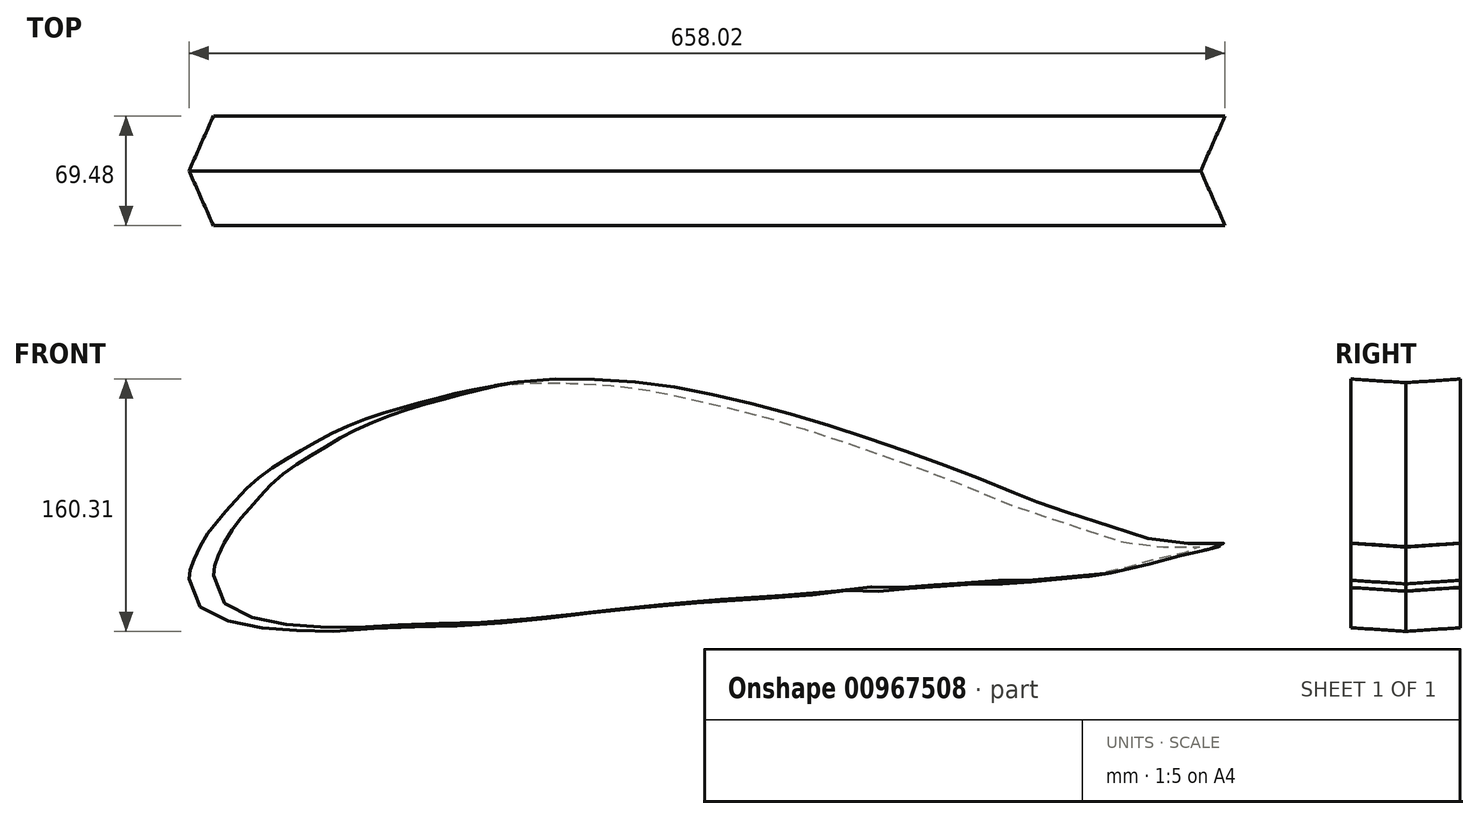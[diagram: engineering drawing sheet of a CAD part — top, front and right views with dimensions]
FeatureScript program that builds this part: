
annotation { "Feature Type Name" : "Feature", "Feature Type Description" : "" }
export const myFeature = defineFeature(function(context is Context, id is Id, definition is map)
    precondition{}
    {
        {
            var Q0;
            Q0=qCreatedBy(makeId("Front.planeOp"),FACE);
            var sketch = newSketch(context, id + "F0", { "sketchPlane" : qUnion([Q0])});
            skFitSpline(sketch, "E0", {"points": [v(4.05, 45.31) * mm, v(5.78, 54.54) * mm, v(15, 73) * mm, v(28.27, 89.14) * mm, v(45.57, 107.6) * mm, v(69.8, 123.74) * mm, v(96.32, 138.73) * mm, v(129.76, 151.42) * mm, v(163.21, 160.64) * mm, v(201.85, 168.72) * mm, v(240.48, 169.87) * mm, v(284.3, 166.99) * mm, v(323.52, 159.5) * mm, v(366.2, 149.11) * mm, v(407.72, 136.42) * mm, v(448.08, 122.58) * mm, v(486.14, 108.75) * mm, v(519.67, 94.87) * mm, v(531.8, 90.25) * mm, v(577.47, 75.22) * mm, v(615.05, 65.97) * mm, v(646.55, 65.4) * mm, v(633.55, 61.34) * mm, v(611, 56.14) * mm, v(577.47, 47.47) * mm, v(527.76, 42.85) * mm, v(519.67, 42.27) * mm, v(503.48, 42.27) * mm, v(481.52, 40.54) * mm, v(463.02, 39.38) * mm, v(444.52, 37.64) * mm, v(424.87, 38.22) * mm, v(404.64, 35.91) * mm, v(343.94, 31.29) * mm, v(280.36, 26.08) * mm, v(239.9, 21.46) * mm, v(201.16, 17.41) * mm, v(162.43, 15.1) * mm, v(130.06, 14.52) * mm, v(97.7, 12.21) * mm, v(71.08, 12.8) * mm, v(48.06, 14.52) * mm, v(25.62, 19.7) * mm, v(10.08, 28.9) * mm, v(4.05, 45.31) * mm]});
            skSolve(sketch);
        }
        {
            var Q0;
            Q0=qCreatedBy(makeId("Top.planeOp"),FACE);
            var sketch = newSketch(context, id + "F1", { "sketchPlane" : qUnion([Q0])});
            skLineSegment(sketch, "E1", {"start": v(4.05, -110.52) * mm, "end": v(4.05, 165.75) * mm, "construction": true});
            skPoint(sketch, "E2", {"position": v(4.05, 0) * mm});
            skLineSegment(sketch, "E3", {"start": v(4.05, 0) * mm, "end": v(18.19, 31.75) * mm});
            skLineSegment(sketch, "E4", {"start": v(4.05, 0) * mm, "end": v(134.8, 0) * mm, "construction": true});
            skLineSegment(sketch, "E5", {"start": v(18.19, 0) * mm, "end": v(18.19, 31.75) * mm, "construction": true});
            skSolve(sketch);
        }
        {
            var Q0;
            Q0=sQuery(id+"F1.wireOp",EDGE,"E3");
            var Q1;
            Q1=sQuery(id+"F1.wireOp",EDGE,"E1");
            cPlane(context, id + "F2", {"entities" : qUnion([Q0, Q1]), "cplaneType" : CPlaneType.LINE_ANGLE, "offset" : 25.4 * mm, "angle" : 90 * degree, "width" : 152.4 * mm, "height" : 152.4 * mm});
        }
        {
            var Q0;
            Q0=qCreatedBy(id+"F2.planeOp",FACE);
            var sketch = newSketch(context, id + "F3", { "sketchPlane" : qUnion([Q0])});
            skLineSegment(sketch, "E6.0", {"start": v(1.65, 0) * mm, "end": v(36.4, 0) * mm, "construction": true});
            skLineSegment(sketch, "E7", {"start": v(1.65, 0) * mm, "end": v(39.68, 2.33) * mm});
            skSolve(sketch);
        }
        {
            var Q0;
            Q0=qSketchRegion(id+"F0",true);
            var Q1;
            Q1=qConstructionFilter(qBodyType(qCreatedBy(id+"F3",EDGE),BodyType.WIRE),ConstructionObject.NO);
            sweep(context, id + "F4", {"profiles" : qUnion([Q0]), "path" : qUnion([Q1])});
        }
        {
            var Q0;
            Q0=makeQuery(id+"F4.opSweep","SWEPT_BODY",BODY,{"disambiguationData":[OSD([sQuery(id+"F0.wireOp",EDGE,"E0"),sQuery(id+"F3.wireOp",EDGE,"l7S8t43I-mMNO-KOTq-Vje2-cWVaEwsp7xa0")])]});
            var Q1;
            Q1=qCreatedBy(makeId("Front.planeOp"),FACE);
            mirror(context, id + "F5", {"entities" : qUnion([Q0]), "mirrorPlane" : qUnion([Q1])});
        }
    });
